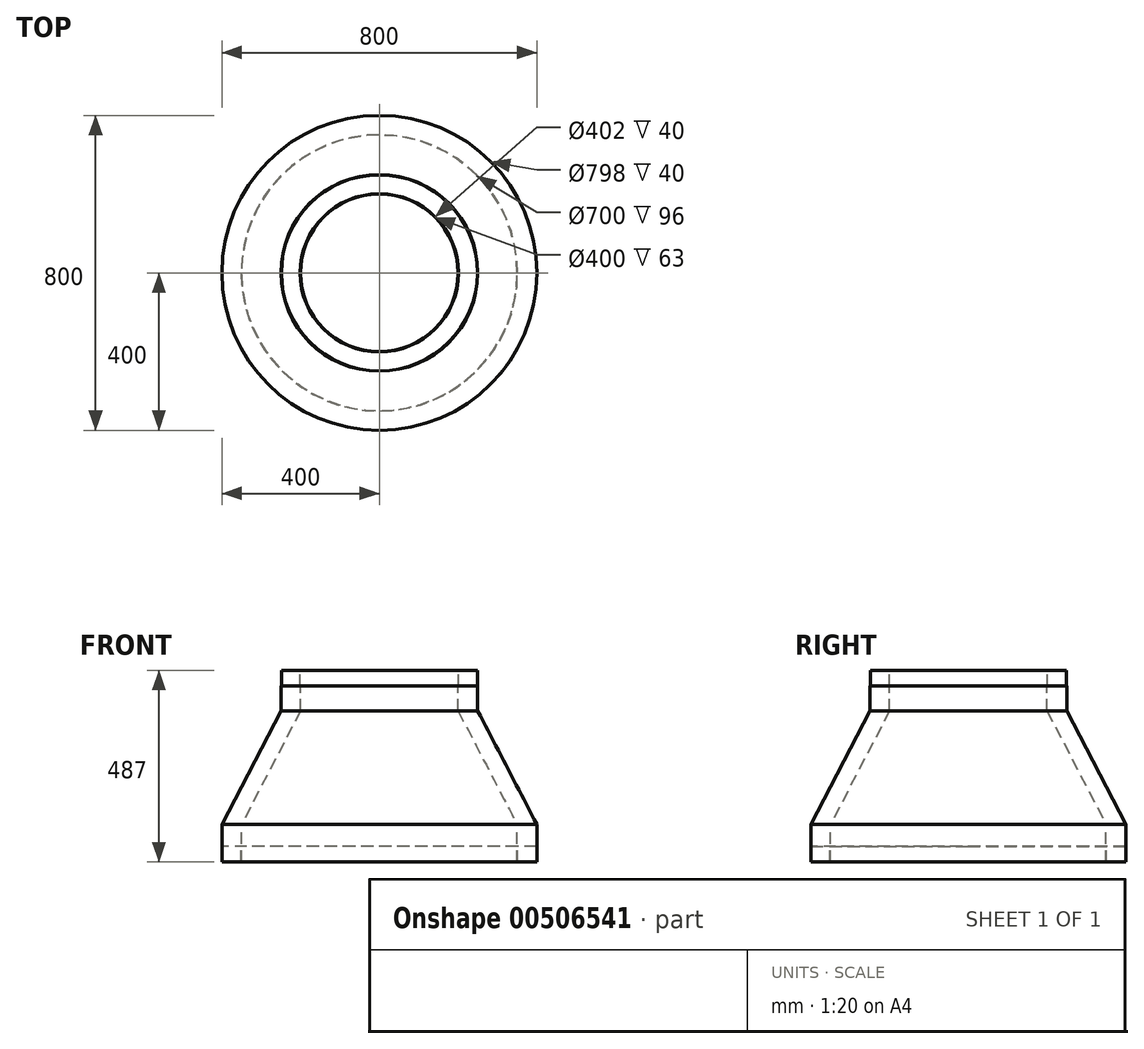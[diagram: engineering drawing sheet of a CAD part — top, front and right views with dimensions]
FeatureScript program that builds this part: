
annotation { "Feature Type Name" : "Feature", "Feature Type Description" : "" }
export const myFeature = defineFeature(function(context is Context, id is Id, definition is map)
    precondition{}
    {
        {
            var Q0;
            Q0=qCreatedBy(makeId("Front.planeOp"),FACE);
            var sketch = newSketch(context, id + "F0", { "sketchPlane" : qUnion([Q0])});
            skLineSegment(sketch, "E0", {"start": v(0, 433.08) * mm, "end": v(0, -434.74) * mm, "construction": true});
            skLineSegment(sketch, "E1", {"start": v(-350, -248.87) * mm, "end": v(-350, -152.87) * mm});
            skLineSegment(sketch, "E2", {"start": v(-350, -248.87) * mm, "end": v(-351, -248.87) * mm});
            skLineSegment(sketch, "E3", {"start": v(-351, -248.87) * mm, "end": v(-351, -208.87) * mm});
            skLineSegment(sketch, "E4", {"start": v(-351, -208.87) * mm, "end": v(-399, -208.87) * mm});
            skLineSegment(sketch, "E5", {"start": v(-399, -208.87) * mm, "end": v(-399, -248.87) * mm});
            skLineSegment(sketch, "E6", {"start": v(-399, -248.87) * mm, "end": v(-400, -248.87) * mm});
            skLineSegment(sketch, "E7", {"start": v(-400, -248.87) * mm, "end": v(-400, -152.87) * mm});
            skLineSegment(sketch, "E8", {"start": v(-249, 238.13) * mm, "end": v(-201, 238.13) * mm});
            skLineSegment(sketch, "E9", {"start": v(-201, 238.13) * mm, "end": v(-201, 198.13) * mm});
            skLineSegment(sketch, "E10", {"start": v(-201, 198.13) * mm, "end": v(-200, 198.13) * mm});
            skLineSegment(sketch, "E11", {"start": v(-200, 198.13) * mm, "end": v(-200, 135.13) * mm});
            skLineSegment(sketch, "E12", {"start": v(-249, 238.13) * mm, "end": v(-249, 198.13) * mm});
            skLineSegment(sketch, "E13", {"start": v(-249, 198.13) * mm, "end": v(-250, 198.13) * mm});
            skLineSegment(sketch, "E14", {"start": v(-250, 198.13) * mm, "end": v(-250, 135.13) * mm});
            skLineSegment(sketch, "E15", {"start": v(-200, 135.13) * mm, "end": v(-350, -152.87) * mm});
            skLineSegment(sketch, "E16", {"start": v(-250, 135.13) * mm, "end": v(-400, -152.87) * mm});
            skSolve(sketch);
        }
        {
            var Q0;
            Q0=qSketchRegion(id+"F0",true);
            var Q1;
            Q1=sQuery(id+"F0.wireOp",EDGE,"E0");
            revolve(context, id + "F1", {"entities" : qUnion([Q0]), "axis" : qUnion([Q1]), "revolveType" : RevolveType.FULL});
        }
    });
